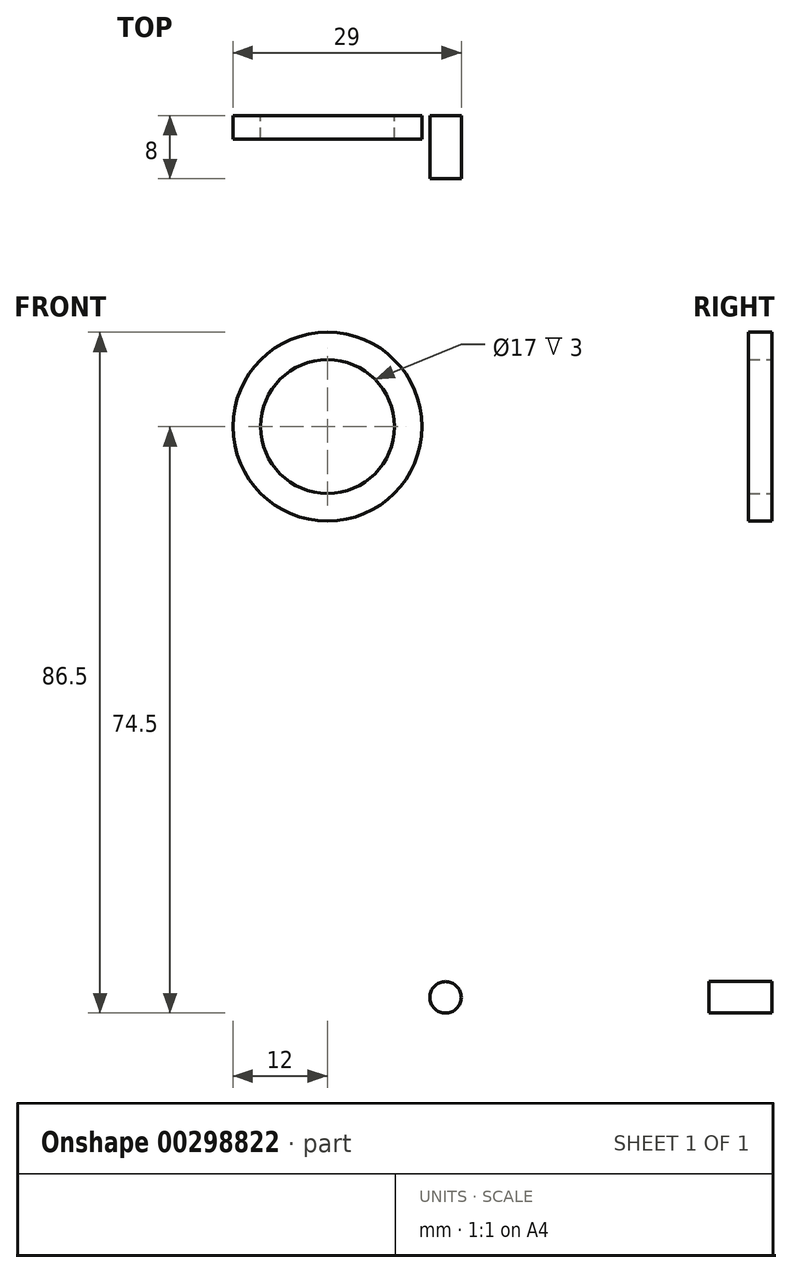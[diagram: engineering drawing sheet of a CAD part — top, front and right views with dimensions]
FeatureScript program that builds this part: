
annotation { "Feature Type Name" : "Feature", "Feature Type Description" : "" }
export const myFeature = defineFeature(function(context is Context, id is Id, definition is map)
    precondition{}
    {
        {
            var Q0;
            Q0=qCreatedBy(makeId("Front.planeOp"),FACE);
            var sketch = newSketch(context, id + "F0", { "sketchPlane" : qUnion([Q0])});
            skArc(sketch, "E0", {"start": v(15.95, -1.24) * mm, "mid": v(0, 16) * mm, "end": v(-15.95, -1.24) * mm});
            skCircle(sketch, "E1", {"center": v(0, 0) * mm, "radius": 12 * mm});
            skLineSegment(sketch, "E2", {"start": v(15.95, -1.24) * mm, "end": v(10.78, -67.5) * mm});
            skLineSegment(sketch, "E3", {"start": v(10, -77.5) * mm, "end": v(-10, -77.5) * mm});
            skLineSegment(sketch, "E4", {"start": v(-10.78, -67.5) * mm, "end": v(-15.95, -1.24) * mm});
            skLineSegment(sketch, "E5", {"start": v(10.78, -67.5) * mm, "end": v(20, -67.5) * mm});
            skLineSegment(sketch, "E6", {"start": v(20, -67.5) * mm, "end": v(20, -77.5) * mm});
            skLineSegment(sketch, "E7", {"start": v(20, -77.5) * mm, "end": v(10, -77.5) * mm});
            skLineSegment(sketch, "E8.MirrorCS", {"start": v(-20, -77.5) * mm, "end": v(-10, -77.5) * mm});
            skLineSegment(sketch, "E9.MirrorCS", {"start": v(-20, -67.5) * mm, "end": v(-20, -77.5) * mm});
            skLineSegment(sketch, "E10.MirrorCS", {"start": v(-10.78, -67.5) * mm, "end": v(-20, -67.5) * mm});
            skSolve(sketch);
        }
        {
            var Q0;
            Q0=makeQuery(id+"F0.imprint","IMPRINT",FACE,{"disambiguationData":[TD([[makeQuery(id+"F0.imprint","IMPRINT",EDGE,{"derivedFrom":sQuery(id+"F0.wireOp",EDGE,"E0")}),1.0]])]});
            extrude(context, id + "F1", {"entities" : qUnion([Q0]), "depth" : 8 * mm});
        }
        {
            var Q0;
            Q0=makeQuery(id+"F1.opExtrude","CAP_FACE",FACE,{"disambiguationData":[OSD([sQuery(id+"F0.wireOp",EDGE,"E0"),sQuery(id+"F0.wireOp",EDGE,"E1"),sQuery(id+"F0.wireOp",EDGE,"E2"),sQuery(id+"F0.wireOp",EDGE,"E3"),sQuery(id+"F0.wireOp",EDGE,"E4"),sQuery(id+"F0.wireOp",EDGE,"E5"),sQuery(id+"F0.wireOp",EDGE,"E6"),sQuery(id+"F0.wireOp",EDGE,"E7"),sQuery(id+"F0.wireOp",EDGE,"E8.MirrorCS"),sQuery(id+"F0.wireOp",EDGE,"E9.MirrorCS"),sQuery(id+"F0.wireOp",EDGE,"E10.MirrorCS")])],"isStart":true});
            var sketch = newSketch(context, id + "F2", { "sketchPlane" : qUnion([Q0])});
            skLineSegment(sketch, "E11", {"start": v(-15.13, -11.81) * mm, "end": v(-7.5, -22.5) * mm});
            skLineSegment(sketch, "E12", {"start": v(-7.5, -22.5) * mm, "end": v(-10.78, -67.5) * mm});
            skLineSegment(sketch, "E13", {"start": v(-10.78, -67.5) * mm, "end": v(-15.13, -11.81) * mm});
            skLineSegment(sketch, "E14.MirrorCS", {"start": v(7.5, -22.5) * mm, "end": v(10.78, -67.5) * mm});
            skLineSegment(sketch, "E15.MirrorCS", {"start": v(10.78, -67.5) * mm, "end": v(15.13, -11.81) * mm});
            skLineSegment(sketch, "E16.MirrorCS", {"start": v(15.13, -11.81) * mm, "end": v(7.5, -22.5) * mm});
            skSolve(sketch);
        }
        {
            var Q0;
            Q0=makeQuery(id+"F2.imprint","IMPRINT",FACE,{"disambiguationData":[TD([[makeQuery(id+"F2.imprint","IMPRINT",EDGE,{"derivedFrom":sQuery(id+"F2.wireOp",EDGE,"E11")}),-1.0]])]});
            var Q1;
            Q1=makeQuery(id+"F2.imprint","IMPRINT",FACE,{"disambiguationData":[TD([[makeQuery(id+"F2.imprint","IMPRINT",EDGE,{"derivedFrom":sQuery(id+"F2.wireOp",EDGE,"E14.MirrorCS")}),1.0]])]});
            extrude(context, id + "F3", {"entities" : qUnion([Q0, Q1]), "operationType" : NewBodyOperationType.REMOVE, "oppositeDirection" : true, "depth" : 25 * mm});
        }
        {
            var Q0;
            Q0=makeQuery(id+"F3.boolean.opBoolean","COPY",EDGE,{"derivedFrom":makeQuery(id+"F3.opExtrude","SWEPT_EDGE",EDGE,{"disambiguationData":[OSD([sQuery(id+"F2.wireOp",EDGE,"E14.MirrorCS"),sQuery(id+"F2.wireOp",EDGE,"E16.MirrorCS")])]})});
            var Q1;
            Q1=makeQuery(id+"F3.boolean.opBoolean","COPY",EDGE,{"derivedFrom":makeQuery(id+"F3.opExtrude","SWEPT_EDGE",EDGE,{"disambiguationData":[OSD([sQuery(id+"F0.wireOp",EDGE,"E4"),sQuery(id+"F2.wireOp",EDGE,"E15.MirrorCS"),sQuery(id+"F2.wireOp",EDGE,"E16.MirrorCS")])]})});
            var Q2;
            Q2=makeQuery(id+"F3.boolean.opBoolean","COPY",EDGE,{"derivedFrom":makeQuery(id+"F3.opExtrude","SWEPT_EDGE",EDGE,{"disambiguationData":[OSD([sQuery(id+"F0.wireOp",EDGE,"E2"),sQuery(id+"F2.wireOp",EDGE,"E11"),sQuery(id+"F2.wireOp",EDGE,"E13")])]})});
            var Q3;
            Q3=makeQuery(id+"F3.boolean.opBoolean","COPY",EDGE,{"derivedFrom":makeQuery(id+"F3.opExtrude","SWEPT_EDGE",EDGE,{"disambiguationData":[OSD([sQuery(id+"F2.wireOp",EDGE,"E11"),sQuery(id+"F2.wireOp",EDGE,"E12")])]})});
            fillet(context, id + "F4", {"entities" : qUnion([Q0, Q1, Q2, Q3]), "radius" : 8 * mm, "tangentPropagation" : true, "allowEdgeOverflow" : false});
        }
        {
            var Q0;
            Q0=makeQuery(id+"F1.opExtrude","CAP_FACE",FACE,{"disambiguationData":[OSD([sQuery(id+"F0.wireOp",EDGE,"E0"),sQuery(id+"F0.wireOp",EDGE,"E1"),sQuery(id+"F0.wireOp",EDGE,"E2"),sQuery(id+"F0.wireOp",EDGE,"E3"),sQuery(id+"F0.wireOp",EDGE,"E4"),sQuery(id+"F0.wireOp",EDGE,"E5"),sQuery(id+"F0.wireOp",EDGE,"E6"),sQuery(id+"F0.wireOp",EDGE,"E7"),sQuery(id+"F0.wireOp",EDGE,"E8.MirrorCS"),sQuery(id+"F0.wireOp",EDGE,"E9.MirrorCS"),sQuery(id+"F0.wireOp",EDGE,"E10.MirrorCS")])],"isStart":true});
            var sketch = newSketch(context, id + "F5", { "sketchPlane" : qUnion([Q0])});
            skCircle(sketch, "E17", {"center": v(0, 0) * mm, "radius": 12 * mm});
            skCircle(sketch, "E18", {"center": v(0, 0) * mm, "radius": 8.5 * mm});
            skSolve(sketch);
        }
        {
            var Q0;
            Q0=makeQuery(id+"F5.imprint","IMPRINT",FACE,{"disambiguationData":[TD([[makeQuery(id+"F5.imprint","IMPRINT",EDGE,{"derivedFrom":sQuery(id+"F5.wireOp",EDGE,"E17")}),-1.0]])]});
            extrude(context, id + "F6", {"entities" : qUnion([Q0]), "operationType" : NewBodyOperationType.ADD, "oppositeDirection" : true, "depth" : 3 * mm});
        }
        {
            var Q0;
            Q0=makeQuery(id+"F1.opExtrude","CAP_FACE",FACE,{"disambiguationData":[OSD([sQuery(id+"F0.wireOp",EDGE,"E0"),sQuery(id+"F0.wireOp",EDGE,"E1"),sQuery(id+"F0.wireOp",EDGE,"E2"),sQuery(id+"F0.wireOp",EDGE,"E3"),sQuery(id+"F0.wireOp",EDGE,"E4"),sQuery(id+"F0.wireOp",EDGE,"E5"),sQuery(id+"F0.wireOp",EDGE,"E6"),sQuery(id+"F0.wireOp",EDGE,"E7"),sQuery(id+"F0.wireOp",EDGE,"E8.MirrorCS"),sQuery(id+"F0.wireOp",EDGE,"E9.MirrorCS"),sQuery(id+"F0.wireOp",EDGE,"E10.MirrorCS")])],"isStart":false});
            var sketch = newSketch(context, id + "F7", { "sketchPlane" : qUnion([Q0])});
            skCircle(sketch, "E19", {"center": v(-15, -72.5) * mm, "radius": 2 * mm});
            skLineSegment(sketch, "E20", {"start": v(-15, -72.5) * mm, "end": v(22.04, -72.5) * mm, "construction": true});
            skCircle(sketch, "E21.MirrorC", {"center": v(15, -72.5) * mm, "radius": 2 * mm});
            skSolve(sketch);
        }
        {
            var Q0;
            Q0=makeQuery(id+"F7.imprint","IMPRINT",FACE,{"disambiguationData":[TD([[makeQuery(id+"F7.imprint","IMPRINT",EDGE,{"derivedFrom":sQuery(id+"F7.wireOp",EDGE,"E19")}),1.0]])]});
            var Q1;
            Q1=makeQuery(id+"F7.imprint","IMPRINT",FACE,{"disambiguationData":[TD([[makeQuery(id+"F7.imprint","IMPRINT",EDGE,{"derivedFrom":sQuery(id+"F7.wireOp",EDGE,"E21.MirrorC")}),-1.0]])]});
            extrude(context, id + "F8", {"entities" : qUnion([Q0, Q1]), "operationType" : NewBodyOperationType.REMOVE, "oppositeDirection" : true, "depth" : 25 * mm});
        }
    });
